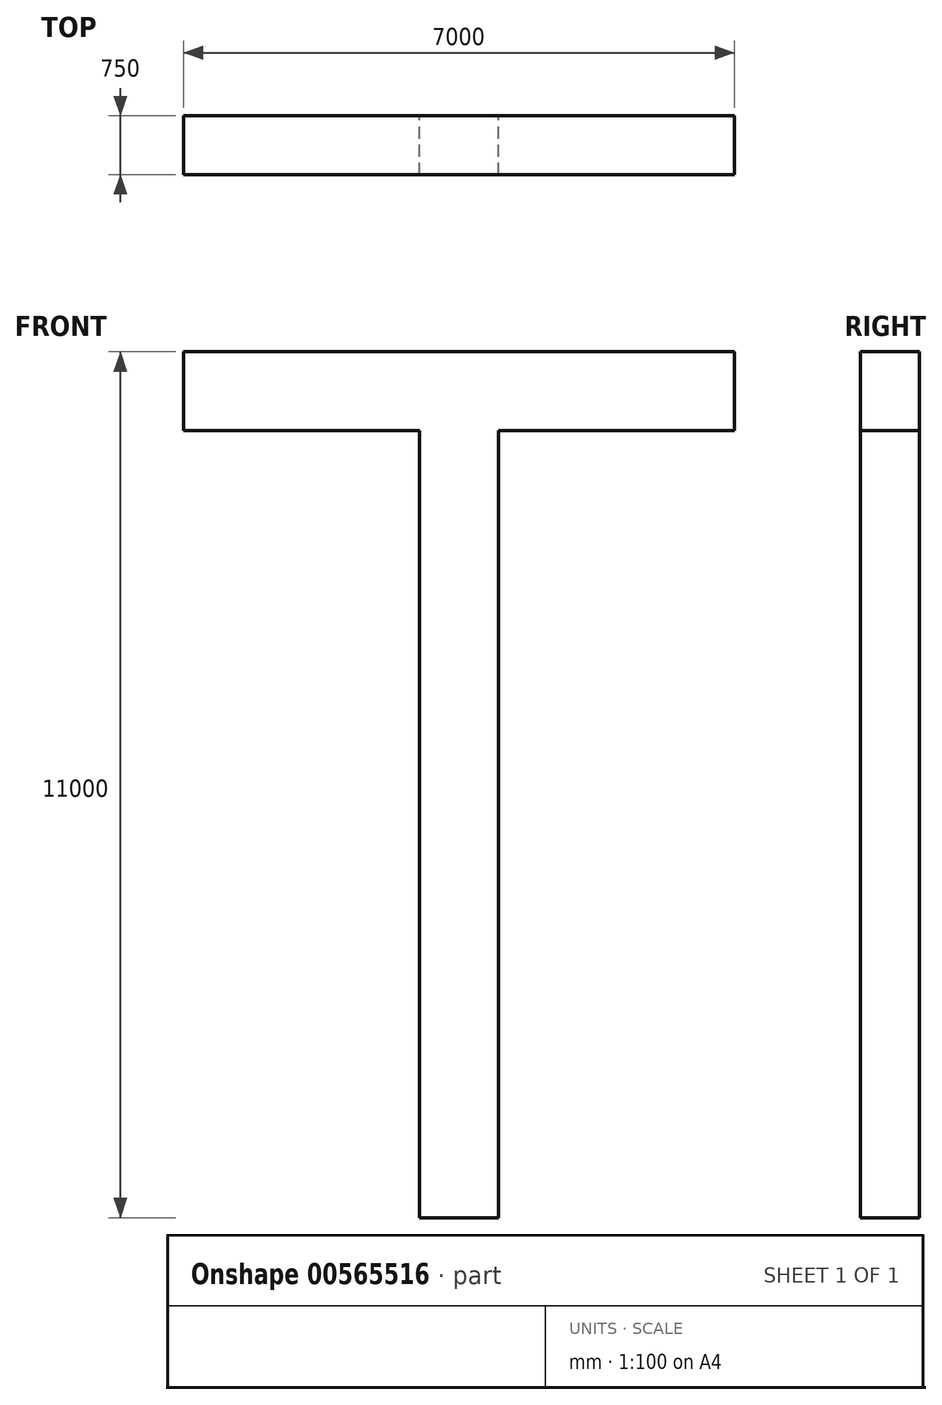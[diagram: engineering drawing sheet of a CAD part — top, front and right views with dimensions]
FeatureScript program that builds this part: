
annotation { "Feature Type Name" : "Feature", "Feature Type Description" : "" }
export const myFeature = defineFeature(function(context is Context, id is Id, definition is map)
    precondition{}
    {
        {
            var Q0;
            Q0=qCreatedBy(makeId("Front.planeOp"),FACE);
            var sketch = newSketch(context, id + "F0", { "sketchPlane" : qUnion([Q0])});
            skLineSegment(sketch, "E0", {"start": v(0, -2726.61) * mm, "end": v(-1000, -2726.61) * mm});
            skLineSegment(sketch, "E1", {"start": v(-1000, -2726.61) * mm, "end": v(-1000, 7273.39) * mm});
            skLineSegment(sketch, "E2", {"start": v(0, -2726.61) * mm, "end": v(0, 7273.39) * mm});
            skLineSegment(sketch, "E3", {"start": v(-1000, 7273.39) * mm, "end": v(-4000, 7273.39) * mm});
            skLineSegment(sketch, "E4", {"start": v(-4000, 7273.39) * mm, "end": v(-4000, 8273.39) * mm});
            skLineSegment(sketch, "E5", {"start": v(-4000, 8273.39) * mm, "end": v(3000, 8273.39) * mm});
            skLineSegment(sketch, "E6", {"start": v(0, 7273.39) * mm, "end": v(3000, 7273.39) * mm});
            skLineSegment(sketch, "E7", {"start": v(3000, 7273.39) * mm, "end": v(3000, 8273.39) * mm});
            skLineSegment(sketch, "E8", {"start": v(-500, 8273.39) * mm, "end": v(-500, 16273.39) * mm});
            skEllipse(sketch, "E9", {"center": v(-500, 12273.39) * mm, "majorRadius": 4000 * mm, "minorRadius": 2250 * mm, "majorAxis": v(0, 1)});
            skLineSegment(sketch, "E10", {"start": v(-500, 12273.39) * mm, "end": v(-2750, 12273.39) * mm});
            skLineSegment(sketch, "E11", {"start": v(-2750, 12273.39) * mm, "end": v(-1625, 12273.39) * mm});
            skLineSegment(sketch, "E12", {"start": v(-2187.5, 12273.39) * mm, "end": v(-1625, 12273.39) * mm});
            skLineSegment(sketch, "E13", {"start": v(-500, 8273.39) * mm, "end": v(-500, 8710.89) * mm});
            skEllipse(sketch, "E14", {"center": v(-500, 12273.39) * mm, "majorRadius": 3562.5 * mm, "minorRadius": 1687.5 * mm, "majorAxis": v(0, -1)});
            skSolve(sketch);
        }
        {
            var Q0;
            Q0=makeQuery(id+"F0.imprint","IMPRINT",FACE,{"disambiguationData":[TD([[makeQuery(id+"F0.imprint","IMPRINT",EDGE,{"derivedFrom":sQuery(id+"F0.wireOp",EDGE,"E0")}),-1.0]])]});
            var Q1;
            {var subQ0=sQuery(id+"F0.wireOp",EDGE,"E11");Q1=makeQuery(id+"F0.imprint","IMPRINT",FACE,{"disambiguationData":[TD([[makeQuery(id+"F0.imprint","IMPRINT",EDGE,{"derivedFrom":subQ0}),-1.0]])]});}
            var Q2;
            {var subQ5=sQuery(id+"F0.wireOp",EDGE,"E13");Q2=makeQuery(id+"F0.imprint","IMPRINT",FACE,{"disambiguationData":[TD([[makeQuery(id+"F0.imprint","IMPRINT",EDGE,{"derivedFrom":subQ5}),-1.0]])]});}
            var Q3;
            {var subQ5=sQuery(id+"F0.wireOp",EDGE,"E11");Q3=makeQuery(id+"F0.imprint","IMPRINT",FACE,{"disambiguationData":[TD([[makeQuery(id+"F0.imprint","IMPRINT",EDGE,{"derivedFrom":subQ5}),1.0]])]});}
            extrude(context, id + "F1", {"entities" : qUnion([Q0, Q1, Q2, Q3]), "depth" : 750 * mm, "offsetDistance" : 25 * mm});
        }
    });
